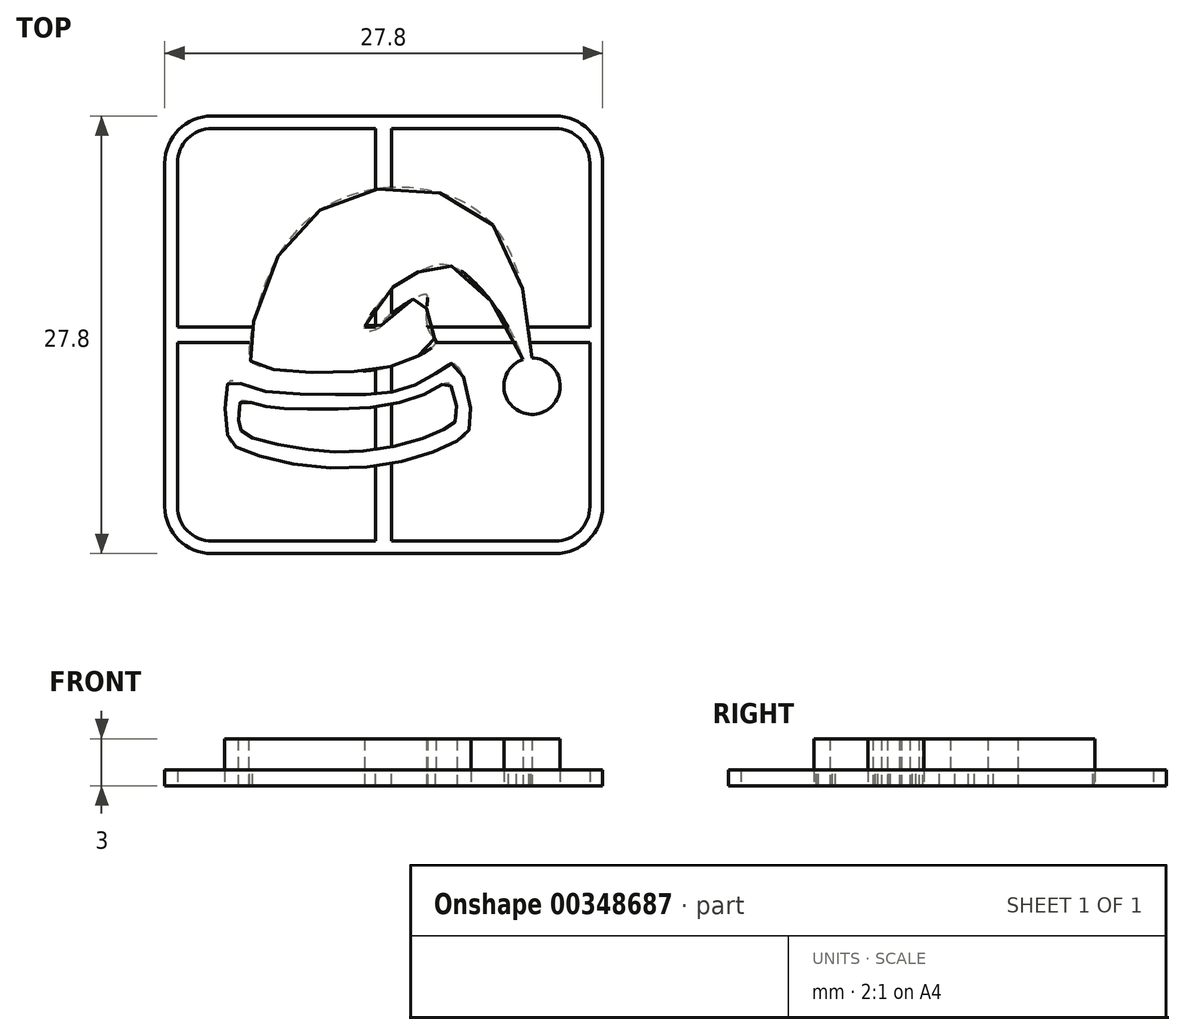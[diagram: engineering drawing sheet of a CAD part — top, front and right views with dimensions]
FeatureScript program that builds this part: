
annotation { "Feature Type Name" : "Feature", "Feature Type Description" : "" }
export const myFeature = defineFeature(function(context is Context, id is Id, definition is map)
    precondition{}
    {
        {
            var Q0;
            Q0=qCreatedBy(makeId("Top.planeOp"),FACE);
            var sketch = newSketch(context, id + "F0", { "sketchPlane" : qUnion([Q0])});
            skLineSegment(sketch, "E0", {"start": v(-13.9, 10.9) * mm, "end": v(-13.9, -10.9) * mm});
            skLineSegment(sketch, "E1", {"start": v(13.9, -10.9) * mm, "end": v(13.9, 10.9) * mm});
            skLineSegment(sketch, "E2", {"start": v(-10.9, 13.9) * mm, "end": v(10.9, 13.9) * mm});
            skLineSegment(sketch, "E3", {"start": v(-10.9, -13.9) * mm, "end": v(10.9, -13.9) * mm});
            skLineSegment(sketch, "E4", {"start": v(0, 13.9) * mm, "end": v(0, -13.9) * mm, "construction": true});
            skLineSegment(sketch, "E5", {"start": v(-13.9, 0) * mm, "end": v(13.9, 0) * mm, "construction": true});
            skPoint(sketch, "E6", {"position": v(0, 0) * mm});
            skPoint(sketch, "E7", {"position": v(0, 13.9) * mm});
            skPoint(sketch, "E8", {"position": v(0, -13.9) * mm});
            skPoint(sketch, "E9", {"position": v(-13.9, 0) * mm});
            skPoint(sketch, "E10", {"position": v(13.9, 0) * mm});
            skArc(sketch, "E11", {"start": v(-10.9, 13.9) * mm, "mid": v(-13.02, 13.02) * mm, "end": v(-13.9, 10.9) * mm});
            skArc(sketch, "E12", {"start": v(13.9, 10.9) * mm, "mid": v(13.02, 13.02) * mm, "end": v(10.9, 13.9) * mm});
            skArc(sketch, "E13", {"start": v(-13.9, -10.9) * mm, "mid": v(-13.02, -13.02) * mm, "end": v(-10.9, -13.9) * mm});
            skArc(sketch, "E14", {"start": v(10.9, -13.9) * mm, "mid": v(13.02, -13.02) * mm, "end": v(13.9, -10.9) * mm});
            skLineSegment(sketch, "E15", {"start": v(-0.5, 13.1) * mm, "end": v(-0.5, 0.5) * mm});
            skLineSegment(sketch, "E16", {"start": v(-0.5, 0.5) * mm, "end": v(-13.1, 0.5) * mm});
            skLineSegment(sketch, "E17", {"start": v(-13.1, 0.5) * mm, "end": v(-13.1, 10.9) * mm});
            skLineSegment(sketch, "E18", {"start": v(-0.5, 13.1) * mm, "end": v(-10.9, 13.1) * mm});
            skArc(sketch, "E19", {"start": v(-10.9, 13.1) * mm, "mid": v(-12.46, 12.46) * mm, "end": v(-13.1, 10.9) * mm});
            skLineSegment(sketch, "E20.MirrorCS", {"start": v(13.1, 0.5) * mm, "end": v(13.1, 10.9) * mm});
            skLineSegment(sketch, "E21.MirrorCS", {"start": v(0.5, 0.5) * mm, "end": v(13.1, 0.5) * mm});
            skLineSegment(sketch, "E22.MirrorCS", {"start": v(0.5, 13.1) * mm, "end": v(10.9, 13.1) * mm});
            skLineSegment(sketch, "E23.MirrorCS", {"start": v(0.5, 13.1) * mm, "end": v(0.5, 0.5) * mm});
            skArc(sketch, "E24.MirrorCS", {"start": v(10.9, 13.1) * mm, "mid": v(12.46, 12.46) * mm, "end": v(13.1, 10.9) * mm});
            skLineSegment(sketch, "E25.MirrorCS", {"start": v(0.5, -13.1) * mm, "end": v(10.9, -13.1) * mm});
            skLineSegment(sketch, "E26.MirrorCS", {"start": v(13.1, -0.5) * mm, "end": v(13.1, -10.9) * mm});
            skArc(sketch, "E27.MirrorCS", {"start": v(10.9, -13.1) * mm, "mid": v(12.46, -12.46) * mm, "end": v(13.1, -10.9) * mm});
            skLineSegment(sketch, "E28.MirrorCS", {"start": v(0.5, -13.1) * mm, "end": v(0.5, -0.5) * mm});
            skLineSegment(sketch, "E29.MirrorCS", {"start": v(0.5, -0.5) * mm, "end": v(13.1, -0.5) * mm});
            skLineSegment(sketch, "E30.MirrorCS", {"start": v(-0.5, -0.5) * mm, "end": v(-13.1, -0.5) * mm});
            skLineSegment(sketch, "E31.MirrorCS", {"start": v(-0.5, -13.1) * mm, "end": v(-0.5, -0.5) * mm});
            skLineSegment(sketch, "E32.MirrorCS", {"start": v(-0.5, -13.1) * mm, "end": v(-10.9, -13.1) * mm});
            skLineSegment(sketch, "E33.MirrorCS", {"start": v(-13.1, -0.5) * mm, "end": v(-13.1, -10.9) * mm});
            skArc(sketch, "E34.MirrorCS", {"start": v(-10.9, -13.1) * mm, "mid": v(-12.46, -12.46) * mm, "end": v(-13.1, -10.9) * mm});
            skSolve(sketch);
        }
        {
            var Q0;
            Q0=makeQuery(id+"F0.imprint","IMPRINT",FACE,{"disambiguationData":[TD([[makeQuery(id+"F0.imprint","IMPRINT",EDGE,{"derivedFrom":sQuery(id+"F0.wireOp",EDGE,"E0")}),1.0]])]});
            extrude(context, id + "F1", {"entities" : qUnion([Q0]), "depth" : 1 * mm});
        }
        {
            var Q0;
            Q0=makeQuery(id+"F1.opExtrude","CAP_FACE",FACE,{"disambiguationData":[OSD([sQuery(id+"F0.wireOp",EDGE,"E0"),sQuery(id+"F0.wireOp",EDGE,"E1"),sQuery(id+"F0.wireOp",EDGE,"E2"),sQuery(id+"F0.wireOp",EDGE,"E3"),sQuery(id+"F0.wireOp",EDGE,"E11"),sQuery(id+"F0.wireOp",EDGE,"E12"),sQuery(id+"F0.wireOp",EDGE,"E13"),sQuery(id+"F0.wireOp",EDGE,"E14"),sQuery(id+"F0.wireOp",EDGE,"E15"),sQuery(id+"F0.wireOp",EDGE,"E16"),sQuery(id+"F0.wireOp",EDGE,"E17"),sQuery(id+"F0.wireOp",EDGE,"E18"),sQuery(id+"F0.wireOp",EDGE,"E19"),sQuery(id+"F0.wireOp",EDGE,"E20.MirrorCS"),sQuery(id+"F0.wireOp",EDGE,"E21.MirrorCS"),sQuery(id+"F0.wireOp",EDGE,"E22.MirrorCS"),sQuery(id+"F0.wireOp",EDGE,"E23.MirrorCS"),sQuery(id+"F0.wireOp",EDGE,"E24.MirrorCS"),sQuery(id+"F0.wireOp",EDGE,"E25.MirrorCS"),sQuery(id+"F0.wireOp",EDGE,"E26.MirrorCS"),sQuery(id+"F0.wireOp",EDGE,"E27.MirrorCS"),sQuery(id+"F0.wireOp",EDGE,"E28.MirrorCS"),sQuery(id+"F0.wireOp",EDGE,"E29.MirrorCS"),sQuery(id+"F0.wireOp",EDGE,"E30.MirrorCS"),sQuery(id+"F0.wireOp",EDGE,"E31.MirrorCS"),sQuery(id+"F0.wireOp",EDGE,"E32.MirrorCS"),sQuery(id+"F0.wireOp",EDGE,"E33.MirrorCS"),sQuery(id+"F0.wireOp",EDGE,"E34.MirrorCS")])],"isStart":false});
            var sketch = newSketch(context, id + "F2", { "sketchPlane" : qUnion([Q0])});
            skFitSpline(sketch, "E35", {"points": [v(-9.37, -7.12) * mm, v(-4.79, -8.34) * mm, v(1.54, -7.94) * mm, v(4.99, -6.53) * mm, v(5.54, -5.36) * mm, v(4.59, -1.88) * mm, v(3.3, -2.45) * mm, v(0.79, -3.57) * mm, v(-2.97, -3.8) * mm, v(-8.52, -3.34) * mm, v(-9.84, -3) * mm, v(-9.96, -6.15) * mm, v(-9.37, -7.12) * mm]});
            skFitSpline(sketch, "E36", {"points": [v(-7.58, -2.07) * mm, v(-5.52, -2.35) * mm, v(-2.95, -2.37) * mm, v(-0.27, -2.18) * mm, v(1.1, -1.78) * mm, v(2.43, -1.22) * mm, v(3.32, -0.43) * mm, v(2.9, 0.23) * mm, v(2.78, 2.13) * mm, v(2.65, 2.57) * mm, v(-0.04, 0.84) * mm, v(-0.24, 0.46) * mm, v(-1.18, 0.28) * mm, v(0.38, 2.8) * mm, v(1.17, 3.43) * mm, v(3, 4.36) * mm, v(4.75, 4.17) * mm, v(8.44, -0.51) * mm, v(9.43, -3.26) * mm, v(9.42, -1.48) * mm, v(7.58, 6.12) * mm, v(2.62, 9.23) * mm, v(-3.27, 8.37) * mm, v(-7.3, 3.81) * mm, v(-8.56, -1.4) * mm, v(-8.37, -1.73) * mm, v(-7.58, -2.07) * mm]});
            skFitSpline(sketch, "E37", {"points": [v(-8.41, -4.31) * mm, v(-9.08, -4.24) * mm, v(-9.21, -5.56) * mm, v(-9.08, -6) * mm, v(-8.6, -6.42) * mm, v(-5.2, -7.23) * mm, v(-1.62, -7.42) * mm, v(2.58, -6.54) * mm, v(4.3, -5.72) * mm, v(4.66, -5.24) * mm, v(4.3, -3.29) * mm, v(4, -3.06) * mm, v(2.61, -3.77) * mm, v(-0.9, -4.6) * mm, v(-5.39, -4.7) * mm, v(-7.27, -4.59) * mm, v(-8.41, -4.31) * mm]});
            skCircle(sketch, "E38", {"center": v(9.43, -3.26) * mm, "radius": 1.79 * mm});
            skSolve(sketch);
        }
        {
            var Q0;
            Q0 = qSketchRegion(id + "F2", true);
            extrude(context, id + "F3", {"entities" : qUnion([Q0]), "operationType" : NewBodyOperationType.ADD, "depth" : 2 * mm});
        }
        {
            var Q0;
            {var subQ0=sQuery(id+"F0.wireOp",EDGE,"E28.MirrorCS");var subQ1=sQuery(id+"F2.wireOp",EDGE,"E35");var subQ2=sQuery(id+"F2.wireOp",EDGE,"E37");Q0=makeQuery(id+"F3.boolean.opBoolean","SPLIT",FACE,{"disambiguationData":[TD([makeQuery(id+"F1.opExtrude","SWEPT_FACE",FACE,{"disambiguationData":[OSD([subQ0])]})])],"derivedFrom":makeQuery(id+"F3.opExtrude","CAP_FACE",FACE,{"disambiguationData":[OSD([subQ1,subQ2])],"isStart":true})});}
            var Q1;
            {var subQ0=sQuery(id+"F0.wireOp",EDGE,"E31.MirrorCS");var subQ1=sQuery(id+"F2.wireOp",EDGE,"E35");var subQ2=sQuery(id+"F2.wireOp",EDGE,"E37");Q1=makeQuery(id+"F3.boolean.opBoolean","SPLIT",FACE,{"disambiguationData":[TD([makeQuery(id+"F1.opExtrude","SWEPT_FACE",FACE,{"disambiguationData":[OSD([subQ0])]})])],"derivedFrom":makeQuery(id+"F3.opExtrude","CAP_FACE",FACE,{"disambiguationData":[OSD([subQ1,subQ2])],"isStart":true})});}
            var Q2;
            {var subQ0=sQuery(id+"F0.wireOp",EDGE,"E31.MirrorCS");var subQ1=sQuery(id+"F0.wireOp",EDGE,"E30.MirrorCS");var subQ2=sQuery(id+"F2.wireOp",EDGE,"E36");Q2=makeQuery(id+"F3.boolean.opBoolean","SPLIT",FACE,{"disambiguationData":[TD([makeQuery(id+"F1.opExtrude","CAP_FACE",FACE,{"disambiguationData":[OSD([sQuery(id+"F0.wireOp",EDGE,"E0"),sQuery(id+"F0.wireOp",EDGE,"E1"),sQuery(id+"F0.wireOp",EDGE,"E2"),sQuery(id+"F0.wireOp",EDGE,"E3"),sQuery(id+"F0.wireOp",EDGE,"E11"),sQuery(id+"F0.wireOp",EDGE,"E12"),sQuery(id+"F0.wireOp",EDGE,"E13"),sQuery(id+"F0.wireOp",EDGE,"E14"),sQuery(id+"F0.wireOp",EDGE,"E15"),sQuery(id+"F0.wireOp",EDGE,"E16"),sQuery(id+"F0.wireOp",EDGE,"E17"),sQuery(id+"F0.wireOp",EDGE,"E18"),sQuery(id+"F0.wireOp",EDGE,"E19"),sQuery(id+"F0.wireOp",EDGE,"E20.MirrorCS"),sQuery(id+"F0.wireOp",EDGE,"E21.MirrorCS"),sQuery(id+"F0.wireOp",EDGE,"E22.MirrorCS"),sQuery(id+"F0.wireOp",EDGE,"E23.MirrorCS"),sQuery(id+"F0.wireOp",EDGE,"E24.MirrorCS"),sQuery(id+"F0.wireOp",EDGE,"E25.MirrorCS"),sQuery(id+"F0.wireOp",EDGE,"E26.MirrorCS"),sQuery(id+"F0.wireOp",EDGE,"E27.MirrorCS"),sQuery(id+"F0.wireOp",EDGE,"E28.MirrorCS"),sQuery(id+"F0.wireOp",EDGE,"E29.MirrorCS"),subQ1,subQ0,sQuery(id+"F0.wireOp",EDGE,"E32.MirrorCS"),sQuery(id+"F0.wireOp",EDGE,"E33.MirrorCS"),sQuery(id+"F0.wireOp",EDGE,"E34.MirrorCS")])],"isStart":false}),makeQuery(id+"F1.opExtrude","SWEPT_FACE",FACE,{"disambiguationData":[OSD([subQ1])]}),makeQuery(id+"F1.opExtrude","SWEPT_FACE",FACE,{"disambiguationData":[OSD([subQ0])]}),makeQuery(id+"F3.opExtrude","SWEPT_FACE",FACE,{"disambiguationData":[OSD([subQ2])]})])],"derivedFrom":makeQuery(id+"F3.opExtrude","CAP_FACE",FACE,{"disambiguationData":[OSD([subQ2,sQuery(id+"F2.wireOp",EDGE,"E38")])],"isStart":true})});}
            var Q3;
            {var subQ0=sQuery(id+"F0.wireOp",EDGE,"E16");var subQ1=sQuery(id+"F0.wireOp",EDGE,"E15");var subQ2=sQuery(id+"F2.wireOp",EDGE,"E36");Q3=makeQuery(id+"F3.boolean.opBoolean","SPLIT",FACE,{"disambiguationData":[TD([makeQuery(id+"F1.opExtrude","CAP_FACE",FACE,{"disambiguationData":[OSD([sQuery(id+"F0.wireOp",EDGE,"E0"),sQuery(id+"F0.wireOp",EDGE,"E1"),sQuery(id+"F0.wireOp",EDGE,"E2"),sQuery(id+"F0.wireOp",EDGE,"E3"),sQuery(id+"F0.wireOp",EDGE,"E11"),sQuery(id+"F0.wireOp",EDGE,"E12"),sQuery(id+"F0.wireOp",EDGE,"E13"),sQuery(id+"F0.wireOp",EDGE,"E14"),subQ1,subQ0,sQuery(id+"F0.wireOp",EDGE,"E17"),sQuery(id+"F0.wireOp",EDGE,"E18"),sQuery(id+"F0.wireOp",EDGE,"E19"),sQuery(id+"F0.wireOp",EDGE,"E20.MirrorCS"),sQuery(id+"F0.wireOp",EDGE,"E21.MirrorCS"),sQuery(id+"F0.wireOp",EDGE,"E22.MirrorCS"),sQuery(id+"F0.wireOp",EDGE,"E23.MirrorCS"),sQuery(id+"F0.wireOp",EDGE,"E24.MirrorCS"),sQuery(id+"F0.wireOp",EDGE,"E25.MirrorCS"),sQuery(id+"F0.wireOp",EDGE,"E26.MirrorCS"),sQuery(id+"F0.wireOp",EDGE,"E27.MirrorCS"),sQuery(id+"F0.wireOp",EDGE,"E28.MirrorCS"),sQuery(id+"F0.wireOp",EDGE,"E29.MirrorCS"),sQuery(id+"F0.wireOp",EDGE,"E30.MirrorCS"),sQuery(id+"F0.wireOp",EDGE,"E31.MirrorCS"),sQuery(id+"F0.wireOp",EDGE,"E32.MirrorCS"),sQuery(id+"F0.wireOp",EDGE,"E33.MirrorCS"),sQuery(id+"F0.wireOp",EDGE,"E34.MirrorCS")])],"isStart":false}),makeQuery(id+"F1.opExtrude","SWEPT_FACE",FACE,{"disambiguationData":[OSD([subQ1])]}),makeQuery(id+"F1.opExtrude","SWEPT_FACE",FACE,{"disambiguationData":[OSD([subQ0])]}),makeQuery(id+"F3.opExtrude","SWEPT_FACE",FACE,{"disambiguationData":[OSD([subQ2])]})])],"derivedFrom":makeQuery(id+"F3.opExtrude","CAP_FACE",FACE,{"disambiguationData":[OSD([subQ2,sQuery(id+"F2.wireOp",EDGE,"E38")])],"isStart":true})});}
            var Q4;
            {var subQ0=sQuery(id+"F0.wireOp",EDGE,"E23.MirrorCS");var subQ1=sQuery(id+"F0.wireOp",EDGE,"E21.MirrorCS");var subQ2=sQuery(id+"F2.wireOp",EDGE,"E36");Q4=makeQuery(id+"F3.boolean.opBoolean","SPLIT",FACE,{"disambiguationData":[TD([makeQuery(id+"F1.opExtrude","CAP_FACE",FACE,{"disambiguationData":[OSD([sQuery(id+"F0.wireOp",EDGE,"E0"),sQuery(id+"F0.wireOp",EDGE,"E1"),sQuery(id+"F0.wireOp",EDGE,"E2"),sQuery(id+"F0.wireOp",EDGE,"E3"),sQuery(id+"F0.wireOp",EDGE,"E11"),sQuery(id+"F0.wireOp",EDGE,"E12"),sQuery(id+"F0.wireOp",EDGE,"E13"),sQuery(id+"F0.wireOp",EDGE,"E14"),sQuery(id+"F0.wireOp",EDGE,"E15"),sQuery(id+"F0.wireOp",EDGE,"E16"),sQuery(id+"F0.wireOp",EDGE,"E17"),sQuery(id+"F0.wireOp",EDGE,"E18"),sQuery(id+"F0.wireOp",EDGE,"E19"),sQuery(id+"F0.wireOp",EDGE,"E20.MirrorCS"),subQ1,sQuery(id+"F0.wireOp",EDGE,"E22.MirrorCS"),subQ0,sQuery(id+"F0.wireOp",EDGE,"E24.MirrorCS"),sQuery(id+"F0.wireOp",EDGE,"E25.MirrorCS"),sQuery(id+"F0.wireOp",EDGE,"E26.MirrorCS"),sQuery(id+"F0.wireOp",EDGE,"E27.MirrorCS"),sQuery(id+"F0.wireOp",EDGE,"E28.MirrorCS"),sQuery(id+"F0.wireOp",EDGE,"E29.MirrorCS"),sQuery(id+"F0.wireOp",EDGE,"E30.MirrorCS"),sQuery(id+"F0.wireOp",EDGE,"E31.MirrorCS"),sQuery(id+"F0.wireOp",EDGE,"E32.MirrorCS"),sQuery(id+"F0.wireOp",EDGE,"E33.MirrorCS"),sQuery(id+"F0.wireOp",EDGE,"E34.MirrorCS")])],"isStart":false}),makeQuery(id+"F1.opExtrude","SWEPT_FACE",FACE,{"disambiguationData":[OSD([subQ1])]}),makeQuery(id+"F1.opExtrude","SWEPT_FACE",FACE,{"disambiguationData":[OSD([subQ0])]}),makeQuery(id+"F3.opExtrude","SWEPT_FACE",FACE,{"disambiguationData":[OSD([subQ2])]})]),OD(1.0)],"derivedFrom":makeQuery(id+"F3.opExtrude","CAP_FACE",FACE,{"disambiguationData":[OSD([subQ2,sQuery(id+"F2.wireOp",EDGE,"E38")])],"isStart":true})});}
            var Q5;
            {var subQ0=sQuery(id+"F0.wireOp",EDGE,"E23.MirrorCS");var subQ1=sQuery(id+"F0.wireOp",EDGE,"E21.MirrorCS");var subQ2=sQuery(id+"F2.wireOp",EDGE,"E36");Q5=makeQuery(id+"F3.boolean.opBoolean","SPLIT",FACE,{"disambiguationData":[TD([makeQuery(id+"F1.opExtrude","CAP_FACE",FACE,{"disambiguationData":[OSD([sQuery(id+"F0.wireOp",EDGE,"E0"),sQuery(id+"F0.wireOp",EDGE,"E1"),sQuery(id+"F0.wireOp",EDGE,"E2"),sQuery(id+"F0.wireOp",EDGE,"E3"),sQuery(id+"F0.wireOp",EDGE,"E11"),sQuery(id+"F0.wireOp",EDGE,"E12"),sQuery(id+"F0.wireOp",EDGE,"E13"),sQuery(id+"F0.wireOp",EDGE,"E14"),sQuery(id+"F0.wireOp",EDGE,"E15"),sQuery(id+"F0.wireOp",EDGE,"E16"),sQuery(id+"F0.wireOp",EDGE,"E17"),sQuery(id+"F0.wireOp",EDGE,"E18"),sQuery(id+"F0.wireOp",EDGE,"E19"),sQuery(id+"F0.wireOp",EDGE,"E20.MirrorCS"),subQ1,sQuery(id+"F0.wireOp",EDGE,"E22.MirrorCS"),subQ0,sQuery(id+"F0.wireOp",EDGE,"E24.MirrorCS"),sQuery(id+"F0.wireOp",EDGE,"E25.MirrorCS"),sQuery(id+"F0.wireOp",EDGE,"E26.MirrorCS"),sQuery(id+"F0.wireOp",EDGE,"E27.MirrorCS"),sQuery(id+"F0.wireOp",EDGE,"E28.MirrorCS"),sQuery(id+"F0.wireOp",EDGE,"E29.MirrorCS"),sQuery(id+"F0.wireOp",EDGE,"E30.MirrorCS"),sQuery(id+"F0.wireOp",EDGE,"E31.MirrorCS"),sQuery(id+"F0.wireOp",EDGE,"E32.MirrorCS"),sQuery(id+"F0.wireOp",EDGE,"E33.MirrorCS"),sQuery(id+"F0.wireOp",EDGE,"E34.MirrorCS")])],"isStart":false}),makeQuery(id+"F1.opExtrude","SWEPT_FACE",FACE,{"disambiguationData":[OSD([subQ1])]}),makeQuery(id+"F1.opExtrude","SWEPT_FACE",FACE,{"disambiguationData":[OSD([subQ0])]}),makeQuery(id+"F3.opExtrude","SWEPT_FACE",FACE,{"disambiguationData":[OSD([subQ2])]})]),OD(0.0)],"derivedFrom":makeQuery(id+"F3.opExtrude","CAP_FACE",FACE,{"disambiguationData":[OSD([subQ2,sQuery(id+"F2.wireOp",EDGE,"E38")])],"isStart":true})});}
            var Q6;
            {var subQ0=sQuery(id+"F0.wireOp",EDGE,"E29.MirrorCS");var subQ1=sQuery(id+"F0.wireOp",EDGE,"E28.MirrorCS");var subQ2=sQuery(id+"F2.wireOp",EDGE,"E36");Q6=makeQuery(id+"F3.boolean.opBoolean","SPLIT",FACE,{"disambiguationData":[TD([makeQuery(id+"F1.opExtrude","CAP_FACE",FACE,{"disambiguationData":[OSD([sQuery(id+"F0.wireOp",EDGE,"E0"),sQuery(id+"F0.wireOp",EDGE,"E1"),sQuery(id+"F0.wireOp",EDGE,"E2"),sQuery(id+"F0.wireOp",EDGE,"E3"),sQuery(id+"F0.wireOp",EDGE,"E11"),sQuery(id+"F0.wireOp",EDGE,"E12"),sQuery(id+"F0.wireOp",EDGE,"E13"),sQuery(id+"F0.wireOp",EDGE,"E14"),sQuery(id+"F0.wireOp",EDGE,"E15"),sQuery(id+"F0.wireOp",EDGE,"E16"),sQuery(id+"F0.wireOp",EDGE,"E17"),sQuery(id+"F0.wireOp",EDGE,"E18"),sQuery(id+"F0.wireOp",EDGE,"E19"),sQuery(id+"F0.wireOp",EDGE,"E20.MirrorCS"),sQuery(id+"F0.wireOp",EDGE,"E21.MirrorCS"),sQuery(id+"F0.wireOp",EDGE,"E22.MirrorCS"),sQuery(id+"F0.wireOp",EDGE,"E23.MirrorCS"),sQuery(id+"F0.wireOp",EDGE,"E24.MirrorCS"),sQuery(id+"F0.wireOp",EDGE,"E25.MirrorCS"),sQuery(id+"F0.wireOp",EDGE,"E26.MirrorCS"),sQuery(id+"F0.wireOp",EDGE,"E27.MirrorCS"),subQ1,subQ0,sQuery(id+"F0.wireOp",EDGE,"E30.MirrorCS"),sQuery(id+"F0.wireOp",EDGE,"E31.MirrorCS"),sQuery(id+"F0.wireOp",EDGE,"E32.MirrorCS"),sQuery(id+"F0.wireOp",EDGE,"E33.MirrorCS"),sQuery(id+"F0.wireOp",EDGE,"E34.MirrorCS")])],"isStart":false}),makeQuery(id+"F1.opExtrude","SWEPT_FACE",FACE,{"disambiguationData":[OSD([subQ1])]}),makeQuery(id+"F1.opExtrude","SWEPT_FACE",FACE,{"disambiguationData":[OSD([subQ0])]}),makeQuery(id+"F3.opExtrude","SWEPT_FACE",FACE,{"disambiguationData":[OSD([subQ2])]})])],"derivedFrom":makeQuery(id+"F3.opExtrude","CAP_FACE",FACE,{"disambiguationData":[OSD([subQ2,sQuery(id+"F2.wireOp",EDGE,"E38")])],"isStart":true})});}
            var Q7;
            {var subQ0=sQuery(id+"F0.wireOp",EDGE,"E29.MirrorCS");var subQ1=sQuery(id+"F2.wireOp",EDGE,"E36");var subQ2=sQuery(id+"F2.wireOp",EDGE,"E38");Q7=makeQuery(id+"F3.boolean.opBoolean","SPLIT",FACE,{"disambiguationData":[TD([makeQuery(id+"F1.opExtrude","CAP_FACE",FACE,{"disambiguationData":[OSD([sQuery(id+"F0.wireOp",EDGE,"E0"),sQuery(id+"F0.wireOp",EDGE,"E1"),sQuery(id+"F0.wireOp",EDGE,"E2"),sQuery(id+"F0.wireOp",EDGE,"E3"),sQuery(id+"F0.wireOp",EDGE,"E11"),sQuery(id+"F0.wireOp",EDGE,"E12"),sQuery(id+"F0.wireOp",EDGE,"E13"),sQuery(id+"F0.wireOp",EDGE,"E14"),sQuery(id+"F0.wireOp",EDGE,"E15"),sQuery(id+"F0.wireOp",EDGE,"E16"),sQuery(id+"F0.wireOp",EDGE,"E17"),sQuery(id+"F0.wireOp",EDGE,"E18"),sQuery(id+"F0.wireOp",EDGE,"E19"),sQuery(id+"F0.wireOp",EDGE,"E20.MirrorCS"),sQuery(id+"F0.wireOp",EDGE,"E21.MirrorCS"),sQuery(id+"F0.wireOp",EDGE,"E22.MirrorCS"),sQuery(id+"F0.wireOp",EDGE,"E23.MirrorCS"),sQuery(id+"F0.wireOp",EDGE,"E24.MirrorCS"),sQuery(id+"F0.wireOp",EDGE,"E25.MirrorCS"),sQuery(id+"F0.wireOp",EDGE,"E26.MirrorCS"),sQuery(id+"F0.wireOp",EDGE,"E27.MirrorCS"),sQuery(id+"F0.wireOp",EDGE,"E28.MirrorCS"),subQ0,sQuery(id+"F0.wireOp",EDGE,"E30.MirrorCS"),sQuery(id+"F0.wireOp",EDGE,"E31.MirrorCS"),sQuery(id+"F0.wireOp",EDGE,"E32.MirrorCS"),sQuery(id+"F0.wireOp",EDGE,"E33.MirrorCS"),sQuery(id+"F0.wireOp",EDGE,"E34.MirrorCS")])],"isStart":false}),makeQuery(id+"F1.opExtrude","SWEPT_FACE",FACE,{"disambiguationData":[OSD([subQ0])]}),makeQuery(id+"F3.opExtrude","SWEPT_FACE",FACE,{"disambiguationData":[OSD([subQ1])]}),makeQuery(id+"F3.opExtrude","SWEPT_FACE",FACE,{"disambiguationData":[OSD([subQ2])]})])],"derivedFrom":makeQuery(id+"F3.opExtrude","CAP_FACE",FACE,{"disambiguationData":[OSD([subQ1,subQ2])],"isStart":true})});}
            extrude(context, id + "F4", {"entities" : qUnion([Q0, Q1, Q2, Q3, Q4, Q5, Q6, Q7]), "operationType" : NewBodyOperationType.ADD, "depth" : 1 * mm});
        }
    });
